# Revit family: LZ.OPL ECO LED TH
name_source: partatom
category: Осветительные приборы
revit_build: Autodesk Revit 2016 (Build: 20150220_1215(x64)
units: mm (PartAtom-declared; Revit-internal decimal feet)

## family parameters
Источник света = Да
Общий = Нет
Основа = Грань
При загрузке вырезать с полостями = Нет
Размер круглого соединителя = Использовать диаметр
Тип детали = Нормальный
Точка расчета площади = Нет

## types (2) — shared parameters
ADSK_Единица измерения = Шт.
ADSK_Завод-изготовитель = ООО МГК Световые технологии
ADSK_Количество фаз = 1
ADSK_Количество фаз числовое = 1
ADSK_Коэффициент мощности = 0.9
ADSK_Масса = 2.4
ADSK_Наименование = Промышленный светильник в узком корпусе (TH) для освещения небольших технических помещений, автомастерских и паркингов. Быстрая и удобная монтаж на опорную поверхность благодаря монтажным пластинам
ADSK_Напряжение = 230 В
ADSK_Номинальная мощность = 0 кВт
ADSK_Полная мощность = 0 кВ·А
ADSK_Размер_Высота = 103 мм
ADSK_Размер_Длина = 1270 мм
ADSK_Размер_Ширина = 110 мм
ADSK_Ток = 0 А
ADSK_Энергоэффективность = 100 лм/Вт
IP Class = IP65
URL = https://www.ltcompany.com
Блок аварийного питания = Нет
Видимая форма излучения при визуализации = Нет
Группа модели = Светильники
Изготовитель = ООО МГК Световые технологии
Излучение по длине прямоугольника = 1270 мм
Излучение по ширине прямоугольника = 110 мм
Класс Защиты = II
Класс пожароопасности = П-I,II,IIa,ІІІ
Климатическая зона = УХЛ2
Код по классификатору = D5020200
Корпус = Серый пластик
Крепление = 5 мм
Область использования = Промышленные предприятия, Складские объекты
Описание = Промышленный светильник в узком корпусе (TH) для освещения небольших технических помещений, автомастерских и паркингов. Быстрая и удобная монтаж на опорную поверхность благодаря монтажным пластинам
Плафон = Плафон самосвечение
Подвес ширина = 800 мм
Полная установленная мощность = 0 кВ·А
Разработчик = ООО ПРОРУБИМ
Разработчик (телефон) = +7 (495) 649-85-43
Светофильтр = 16777215
Смещение цветовой температуры при затухании лампы = <Нет>
Тип ИС = LED
Тип продукции = Светильник
Угол наклона = -90.00°
Файл фотометрической сетки = LZ.OPL ECO LED 1200 TH 5000K.ies
zero-valued in all types: Отметка по умолчанию

## per-type parameters (varying)
| type | ADSK_Код изделия | Подвес.материал | Тип ПРА |
| LZ.OPL ECO LED 1200 TH 5000K | 1074000460 | <По категории> | Драйвер |
| LZ.OPL ECO LED 1200 TH HFD 5000K | 1074000560 | Корпус металл | Драйвер DALI |

## geometry (parser evidence)
native form markers: Blend x2
no freeform markers — native parametric forms only
